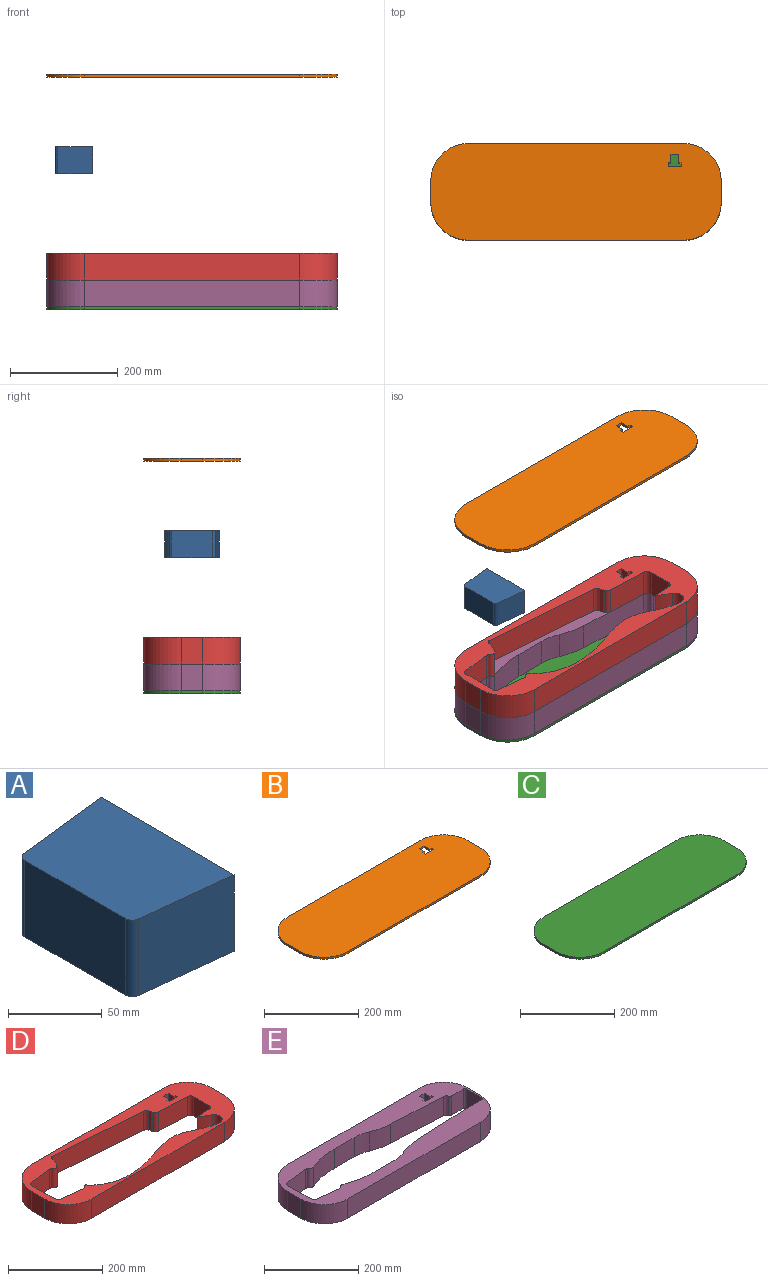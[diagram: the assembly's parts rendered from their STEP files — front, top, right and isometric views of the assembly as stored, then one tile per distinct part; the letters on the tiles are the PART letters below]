
ASSEMBLY  parts=5 mates=4
PART A: 10 faces, bbox 70x100.8x50 mm
  f0: plane 50.37x50mm, normal (1,-0.01,0), area 2518.6mm2, adj f1,f7,f8,f9
  f1: plane 50.4x50mm, normal (1,0,0), area 2520.1mm2, adj f0,f2,f8,f9
  f2: cylinder r=5mm len=50mm, axis (0,0,1), area 28.6mm2, adj f1,f3,f8,f9
  f3: plane 64.99x50mm, normal (-0.11,0.99,0), area 3270.4mm2, adj f2,f4,f8,f9
  f4: cylinder r=5mm len=50mm, axis (0,0,1), area 364.5mm2, adj f3,f5,f8,f9
  f5: plane 76.07x50mm, normal (-1,0,0), area 3803.5mm2, adj f4,f6,f8,f9
  f6: cylinder r=5mm len=50mm, axis (0,0,1), area 364.5mm2, adj f5,f7,f8,f9
  f7: plane 64.99x50mm, normal (-0.11,-0.99,0), area 3270.4mm2, adj f0,f6,f8,f9
  f8: plane 100.77x70mm, normal (0,0,-1), area 6482.8mm2, adj f0,f1,f2,f3,f4,f5,f6,f7
  f9: plane 100.77x70mm, normal (0,0,1), area 6482.8mm2, adj f0,f1,f2,f3,f4,f5,f6,f7
PART B: 18 faces, bbox 540x180x5 mm
  f0: plane 7x5mm, normal (1,0,0), area 35mm2, adj f1,f15,f16,f17
  f1: plane 5.5x5mm, normal (0,-1,0), area 27.5mm2, adj f0,f2,f16,f17
  f2: plane 16x5mm, normal (1,0,0), area 80mm2, adj f1,f3,f16,f17
  f3: plane 14x5mm, normal (0,-1,0), area 70mm2, adj f2,f4,f16,f17
  f4: plane 16x5mm, normal (-1,0,0), area 80mm2, adj f3,f5,f16,f17
  f5: plane 5.5x5mm, normal (0,-1,0), area 27.5mm2, adj f4,f6,f16,f17
  f6: plane 7x5mm, normal (-1,0,0), area 35mm2, adj f5,f15,f16,f17
  f7: plane 400x5mm, normal (0,1,0), area 2000mm2, adj f8,f14,f16,f17
  f8: cylinder r=70mm len=70mm, axis (0,0,-1), area 549.8mm2, adj f7,f9,f16,f17
  f9: plane 40x5mm, normal (-1,0,0), area 200mm2, adj f8,f10,f16,f17
  f10: cylinder r=70mm len=70mm, axis (0,0,-1), area 549.8mm2, adj f9,f11,f16,f17
  f11: plane 400x5mm, normal (0,-1,0), area 2000mm2, adj f10,f12,f16,f17
  f12: cylinder r=70mm len=70mm, axis (0,0,-1), area 549.8mm2, adj f11,f13,f16,f17
  f13: plane 40x5mm, normal (1,0,0), area 200mm2, adj f12,f14,f16,f17
  f14: cylinder r=70mm len=70mm, axis (0,0,-1), area 549.8mm2, adj f7,f13,f16,f17
  f15: plane 25x5mm, normal (0,1,0), area 125mm2, adj f0,f6,f16,f17
  f16: plane 540x180mm, normal (0,0,1), area 92594.8mm2, adj f0,f1,f2,f3,f4,f5,f6,f7
  f17: plane 540x180mm, normal (0,0,-1), area 92594.8mm2, adj f0,f1,f2,f3,f4,f5,f6,f7
PART C: 10 faces, bbox 540x180x5 mm
  f0: cylinder r=70mm len=70mm, axis (0,0,1), area 549.8mm2, adj f1,f7,f8,f9
  f1: plane 400x5mm, normal (0,1,0), area 2000mm2, adj f0,f2,f8,f9
  f2: cylinder r=70mm len=70mm, axis (0,0,1), area 549.8mm2, adj f1,f3,f8,f9
  f3: plane 40x5mm, normal (1,0,0), area 200mm2, adj f2,f4,f8,f9
  f4: cylinder r=70mm len=70mm, axis (0,0,1), area 549.8mm2, adj f3,f5,f8,f9
  f5: plane 400x5mm, normal (0,-1,0), area 2000mm2, adj f4,f6,f8,f9
  f6: cylinder r=70mm len=70mm, axis (0,0,1), area 549.8mm2, adj f5,f7,f8,f9
  f7: plane 40x5mm, normal (-1,0,0), area 200mm2, adj f0,f6,f8,f9
  f8: plane 540x180mm, normal (0,0,-1), area 92993.8mm2, adj f0,f1,f2,f3,f4,f5,f6,f7
  f9: plane 540x180mm, normal (0,0,1), area 92993.8mm2, adj f0,f1,f2,f3,f4,f5,f6,f7
PART D: 59 faces, bbox 540x180x50 mm
  f0: plane 540x180mm, normal (0,0,1), area 34830.6mm2, adj f2,f3,f4,f5,f6,f7,f8,f9
  f1: plane 540x180mm, normal (0,0,-1), area 34830.6mm2, adj f2,f3,f4,f5,f6,f7,f8,f9
  f2: cylinder r=70.8mm len=50mm, axis (0,0,1), area 324.2mm2, adj f0,f1,f17,f40
  f3: cylinder r=163.54mm len=50mm, axis (0,0,1), area 132.1mm2, adj f0,f1,f33,f50
  f4: plane 400x50mm, normal (0,1,0), area 20000mm2, adj f0,f1,f5,f11
  f5: cylinder r=70mm len=70mm, axis (0,0,-1), area 5497.8mm2, adj f0,f1,f4,f6
  f6: plane 50x40mm, normal (-1,0,0), area 2000mm2, adj f0,f1,f5,f7
  f7: cylinder r=70mm len=70mm, axis (0,0,-1), area 5497.8mm2, adj f0,f1,f6,f8
  f8: plane 400x50mm, normal (0,-1,0), area 20000mm2, adj f0,f1,f7,f9
  f9: cylinder r=70mm len=70mm, axis (0,0,-1), area 5497.8mm2, adj f0,f1,f8,f10
  f10: plane 50x40mm, normal (1,0,0), area 2000mm2, adj f0,f1,f9,f11
  f11: cylinder r=70mm len=70mm, axis (0,0,-1), area 5497.8mm2, adj f0,f1,f4,f10
  f12: plane 254.43x50mm, normal (-0.08,-1,0), area 12761.1mm2, adj f0,f1,f13,f34
  f13: cylinder r=7.12mm len=50mm, axis (0,0,1), area 489.4mm2, adj f0,f1,f12,f14
  f14: plane 50x4.72mm, normal (0.98,-0.22,0), area 241.6mm2, adj f0,f1,f13,f15
  f15: cylinder r=53.57mm len=50mm, axis (0,0,1), area 881.7mm2, adj f0,f1,f14,f16
  f16: cylinder r=196.58mm len=50mm, axis (0,0,1), area 560mm2, adj f0,f1,f15,f41
  f17: cylinder r=109.79mm len=50mm, axis (0,0,1), area 2580.3mm2, adj f0,f1,f2,f18
  f18: cylinder r=139.49mm len=68.27mm, axis (0,0,1), area 3459.2mm2, adj f0,f1,f17,f19
  f19: cylinder r=188.07mm len=50mm, axis (0,0,1), area 1059.1mm2, adj f0,f1,f18,f20
  f20: cylinder r=186.25mm len=50mm, axis (0,0,1), area 1829.3mm2, adj f0,f1,f19,f21
  f21: cylinder r=285.23mm len=50mm, axis (0,0,1), area 1295.3mm2, adj f0,f1,f20,f22
  f22: cylinder r=206.38mm len=50mm, axis (0,0,1), area 2031.5mm2, adj f0,f1,f21,f23
  f23: cylinder r=98.26mm len=57.35mm, axis (0,0,1), area 2934.9mm2, adj f0,f1,f22,f24
  f24: plane 50x2.26mm, normal (0.41,0.91,0), area 124.1mm2, adj f0,f1,f23,f25
  f25: plane 50x13.3mm, normal (0.41,0.91,0), area 728.8mm2, adj f0,f1,f24,f26
  f26: plane 50x16.85mm, normal (0.39,0.92,0), area 915.8mm2, adj f0,f1,f25,f27
  f27: plane 50x17.22mm, normal (0.35,0.94,0), area 919.1mm2, adj f0,f1,f26,f28
  f28: plane 50x11.39mm, normal (0.29,0.96,0), area 594.5mm2, adj f0,f1,f27,f29
  f29: plane 50x4.21mm, normal (0.14,0.99,0), area 212.6mm2, adj f0,f1,f28,f30
  f30: cylinder r=24.39mm len=50mm, axis (0,0,1), area 958.1mm2, adj f0,f1,f29,f31
  f31: cylinder r=17.17mm len=50mm, axis (0,0,1), area 1522.6mm2, adj f0,f1,f30,f32
  f32: cylinder r=163.54mm len=50mm, axis (0,0,1), area 1685.8mm2, adj f0,f1,f31,f38
  f33: plane 50x6.75mm, normal (-0.97,-0.24,0), area 347.5mm2, adj f0,f1,f3,f34
  f34: cylinder r=10mm len=50mm, axis (0,0,1), area 624.6mm2, adj f0,f1,f12,f33
  f35: plane 83.72x50mm, normal (-0.05,-1,0), area 4191.1mm2, adj f0,f1,f36,f50
  f36: cylinder r=10mm len=50mm, axis (0,0,1), area 761.3mm2, adj f0,f1,f35,f37
  f37: plane 50x45.94mm, normal (-1,0,0), area 2297.1mm2, adj f0,f1,f36,f39
  f38: plane 50x37.78mm, normal (-0.05,1,0), area 1891.4mm2, adj f0,f1,f32,f39
  f39: cylinder r=10mm len=50mm, axis (0,0,1), area 761.3mm2, adj f0,f1,f37,f38
  f40: cylinder r=10mm len=50mm, axis (0,0,1), area 487.6mm2, adj f0,f1,f2,f49
  f41: cylinder r=212.48mm len=50mm, axis (0,0,1), area 1.7mm2, adj f0,f1,f16,f42
  f42: cylinder r=10mm len=50mm, axis (0,0,1), area 659.3mm2, adj f0,f1,f41,f43
  f43: cylinder r=5mm len=50mm, axis (0,0,1), area 263.2mm2, adj f0,f1,f42,f44
  f44: plane 64.99x50mm, normal (0.11,-0.99,0), area 3270.4mm2, adj f0,f1,f43,f45
  f45: cylinder r=5mm len=50mm, axis (0,0,1), area 364.5mm2, adj f0,f1,f44,f46
  f46: plane 76.07x50mm, normal (1,0,0), area 3803.5mm2, adj f0,f1,f45,f47
  f47: cylinder r=5mm len=50mm, axis (0,0,1), area 364.5mm2, adj f0,f1,f46,f48
  f48: plane 64.99x50mm, normal (0.11,0.99,0), area 3270.4mm2, adj f0,f1,f47,f49
  f49: cylinder r=5mm len=50mm, axis (0,0,1), area 263.2mm2, adj f0,f1,f40,f48
  f50: cylinder r=10mm len=50mm, axis (0,0,1), area 605.4mm2, adj f0,f1,f3,f35
  f51: plane 50x5.5mm, normal (0,-1,0), area 275mm2, adj f0,f1,f52,f58
  f52: plane 50x7mm, normal (1,0,0), area 350mm2, adj f0,f1,f51,f53
  f53: plane 50x25mm, normal (0,1,0), area 1250mm2, adj f0,f1,f52,f54
  f54: plane 50x7mm, normal (-1,0,0), area 350mm2, adj f0,f1,f53,f55
  f55: plane 50x5.5mm, normal (0,-1,0), area 275mm2, adj f0,f1,f54,f56
  f56: plane 50x16mm, normal (-1,0,0), area 800mm2, adj f0,f1,f55,f57
  f57: plane 50x14mm, normal (0,-1,0), area 700mm2, adj f0,f1,f56,f58
  f58: plane 50x16mm, normal (1,0,0), area 800mm2, adj f0,f1,f51,f57
PART E: 44 faces, bbox 540x180x50 mm
  f0: plane 540x180mm, normal (0,0,1), area 45635.9mm2, adj f2,f3,f4,f5,f6,f7,f8,f9
  f1: plane 540x180mm, normal (0,0,-1), area 45635.9mm2, adj f2,f3,f4,f5,f6,f7,f8,f9
  f2: plane 400x50mm, normal (0,1,0), area 20000mm2, adj f0,f1,f3,f9
  f3: cylinder r=70mm len=70mm, axis (0,0,-1), area 5497.8mm2, adj f0,f1,f2,f4
  f4: plane 50x40mm, normal (-1,0,0), area 2000mm2, adj f0,f1,f3,f5
  f5: cylinder r=70mm len=70mm, axis (0,0,-1), area 5497.8mm2, adj f0,f1,f4,f6
  f6: plane 400x50mm, normal (0,-1,0), area 20000mm2, adj f0,f1,f5,f7
  f7: cylinder r=70mm len=70mm, axis (0,0,-1), area 5497.8mm2, adj f0,f1,f6,f8
  f8: plane 50x40mm, normal (1,0,0), area 2000mm2, adj f0,f1,f7,f9
  f9: cylinder r=70mm len=70mm, axis (0,0,-1), area 5497.8mm2, adj f0,f1,f2,f8
  f10: cylinder r=10mm len=50mm, axis (0,0,1), area 623.9mm2, adj f0,f1,f11,f35
  f11: plane 150.48x50mm, normal (-0.05,-1,0), area 7532.9mm2, adj f0,f1,f10,f12
  f12: cylinder r=154.31mm len=52.85mm, axis (0,0,1), area 2724.8mm2, adj f0,f1,f11,f13
  f13: cylinder r=96.78mm len=50mm, axis (0,0,1), area 1942.2mm2, adj f0,f1,f12,f14
  f14: plane 60x50mm, normal (0,-1,0), area 3000mm2, adj f0,f1,f13,f15
  f15: cylinder r=212.48mm len=78.53mm, axis (0,0,1), area 4022mm2, adj f0,f1,f14,f33
  f16: cylinder r=212.48mm len=78.53mm, axis (0,0,1), area 4022mm2, adj f0,f1,f17,f34
  f17: plane 60x50mm, normal (0,1,0), area 3000mm2, adj f0,f1,f16,f18
  f18: cylinder r=96.78mm len=50mm, axis (0,0,1), area 1942.2mm2, adj f0,f1,f17,f19
  f19: cylinder r=154.31mm len=52.85mm, axis (0,0,1), area 2724.8mm2, adj f0,f1,f18,f20
  f20: plane 150.48x50mm, normal (-0.05,1,0), area 7532.9mm2, adj f0,f1,f19,f21
  f21: plane 50x49.52mm, normal (0,1,0), area 2475.9mm2, adj f0,f1,f20,f22
  f22: cylinder r=5mm len=50mm, axis (0,0,1), area 392.7mm2, adj f0,f1,f21,f23
  f23: plane 50x45mm, normal (-1,0,0), area 2250mm2, adj f0,f1,f22,f24
  f24: cylinder r=5mm len=50mm, axis (0,0,1), area 392.7mm2, adj f0,f1,f23,f25
  f25: plane 50x35.56mm, normal (0,-1,0), area 1778.1mm2, adj f0,f1,f24,f35
  f26: cylinder r=5mm len=50mm, axis (0,0,1), area 263.2mm2, adj f0,f1,f27,f33
  f27: plane 64.99x50mm, normal (0.11,-0.99,0), area 3270.4mm2, adj f0,f1,f26,f28
  f28: cylinder r=5mm len=50mm, axis (0,0,1), area 364.5mm2, adj f0,f1,f27,f29
  f29: plane 76.07x50mm, normal (1,0,0), area 3803.5mm2, adj f0,f1,f28,f30
  f30: cylinder r=5mm len=50mm, axis (0,0,1), area 364.5mm2, adj f0,f1,f29,f31
  f31: plane 64.99x50mm, normal (0.11,0.99,0), area 3270.4mm2, adj f0,f1,f30,f32
  f32: cylinder r=5mm len=50mm, axis (0,0,1), area 263.2mm2, adj f0,f1,f31,f34
  f33: cylinder r=10mm len=50mm, axis (0,0,1), area 659.3mm2, adj f0,f1,f15,f26
  f34: cylinder r=10mm len=50mm, axis (0,0,1), area 659.3mm2, adj f0,f1,f16,f32
  f35: cylinder r=5mm len=50mm, axis (0,0,1), area 324mm2, adj f0,f1,f10,f25
  f36: plane 50x5.5mm, normal (0,-1,0), area 275mm2, adj f0,f1,f37,f43
  f37: plane 50x7mm, normal (1,0,0), area 350mm2, adj f0,f1,f36,f38
  f38: plane 50x25mm, normal (0,1,0), area 1250mm2, adj f0,f1,f37,f39
  f39: plane 50x7mm, normal (-1,0,0), area 350mm2, adj f0,f1,f38,f40
  f40: plane 50x5.5mm, normal (0,-1,0), area 275mm2, adj f0,f1,f39,f41
  f41: plane 50x16mm, normal (-1,0,0), area 800mm2, adj f0,f1,f40,f42
  f42: plane 50x14mm, normal (0,-1,0), area 700mm2, adj f0,f1,f41,f43
  f43: plane 50x16mm, normal (1,0,0), area 800mm2, adj f0,f1,f36,f42
PLACE A t=(56.49,17.06,53.7)mm
PLACE B t=(56.49,17.06,183.07)mm
PLACE C t=(56.49,17.06,-94.42)mm
PLACE D t=(56.49,17.06,-144.42)mm
PLACE E t=(56.49,17.06,-144.42)mm fixed
MATE slider B.f17 <-> D.f0  axis (0,0,-1) through (52.64,-25.94,303.07)mm
MATE slider A.f8 <-> E.f0  axis (0,0,-1) through (-397.85,-72.96,123.7)mm
MATE fastened E.f1 <-> C.f9  axis (0,0,-1) through (-343.51,-162.94,-124.42)mm
MATE fastened E.f0 <-> D.f1  axis (0,0,1) through (-343.51,-162.94,-74.42)mm
